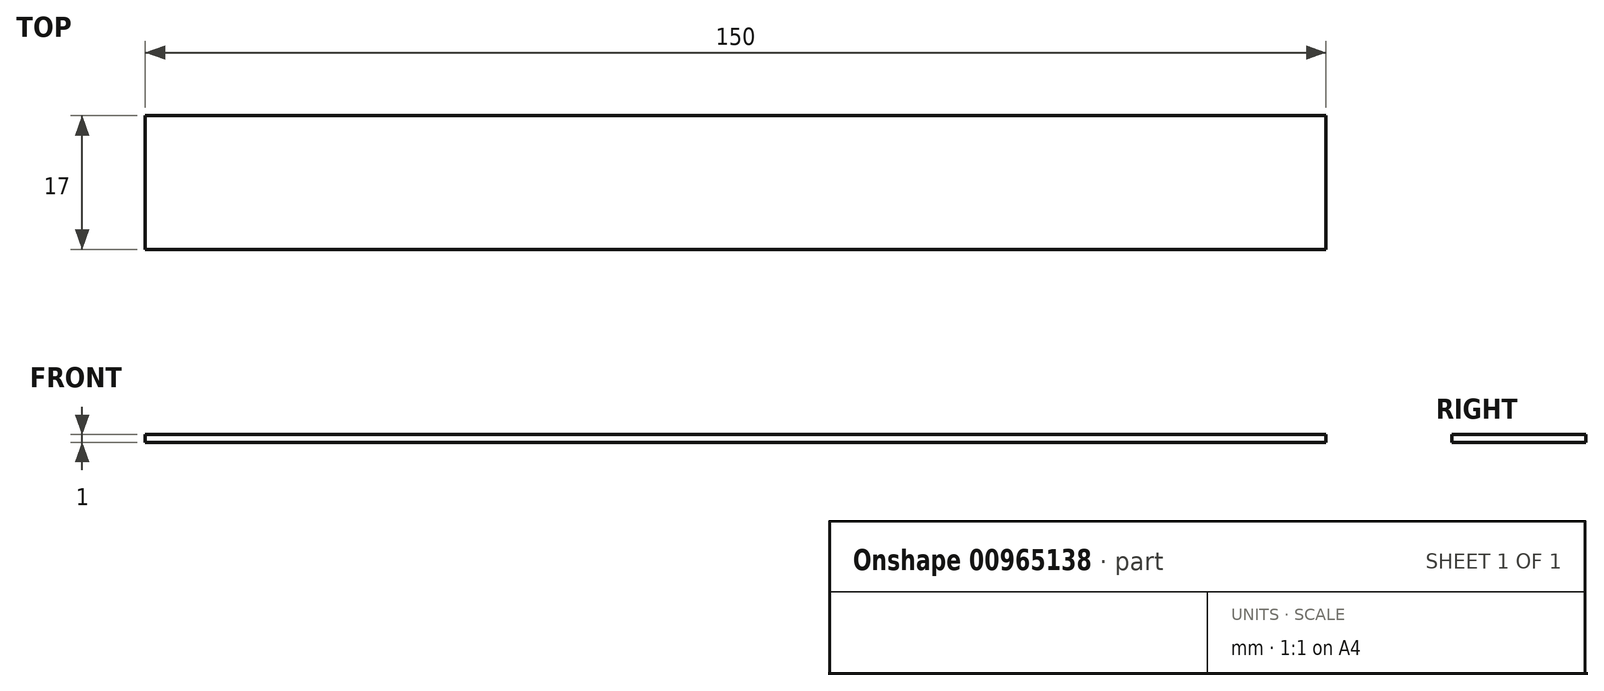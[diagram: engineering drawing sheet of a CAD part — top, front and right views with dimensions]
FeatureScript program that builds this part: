
annotation { "Feature Type Name" : "Feature", "Feature Type Description" : "" }
export const myFeature = defineFeature(function(context is Context, id is Id, definition is map)
    precondition{}
    {
        {
            var Q0;
            Q0=qCreatedBy(makeId("Top.planeOp"),FACE);
            var sketch = newSketch(context, id + "F0", { "sketchPlane" : qUnion([Q0])});
            skLineSegment(sketch, "E0.bottom", {"start": v(-89.9, -30.02) * mm, "end": v(60.1, -30.02) * mm});
            skLineSegment(sketch, "E0.top", {"start": v(-89.9, -47.02) * mm, "end": v(60.1, -47.02) * mm});
            skLineSegment(sketch, "E0.left", {"start": v(-89.9, -30.02) * mm, "end": v(-89.9, -47.02) * mm});
            skLineSegment(sketch, "E0.right", {"start": v(60.1, -30.02) * mm, "end": v(60.1, -47.02) * mm});
            skSolve(sketch);
        }
        {
            var Q0;
            Q0 = qSketchRegion(id + "F0", true);
            extrude(context, id + "F1", {"entities" : qUnion([Q0]), "depth" : 1 * mm, "offsetDistance" : 25 * mm});
        }
    });
